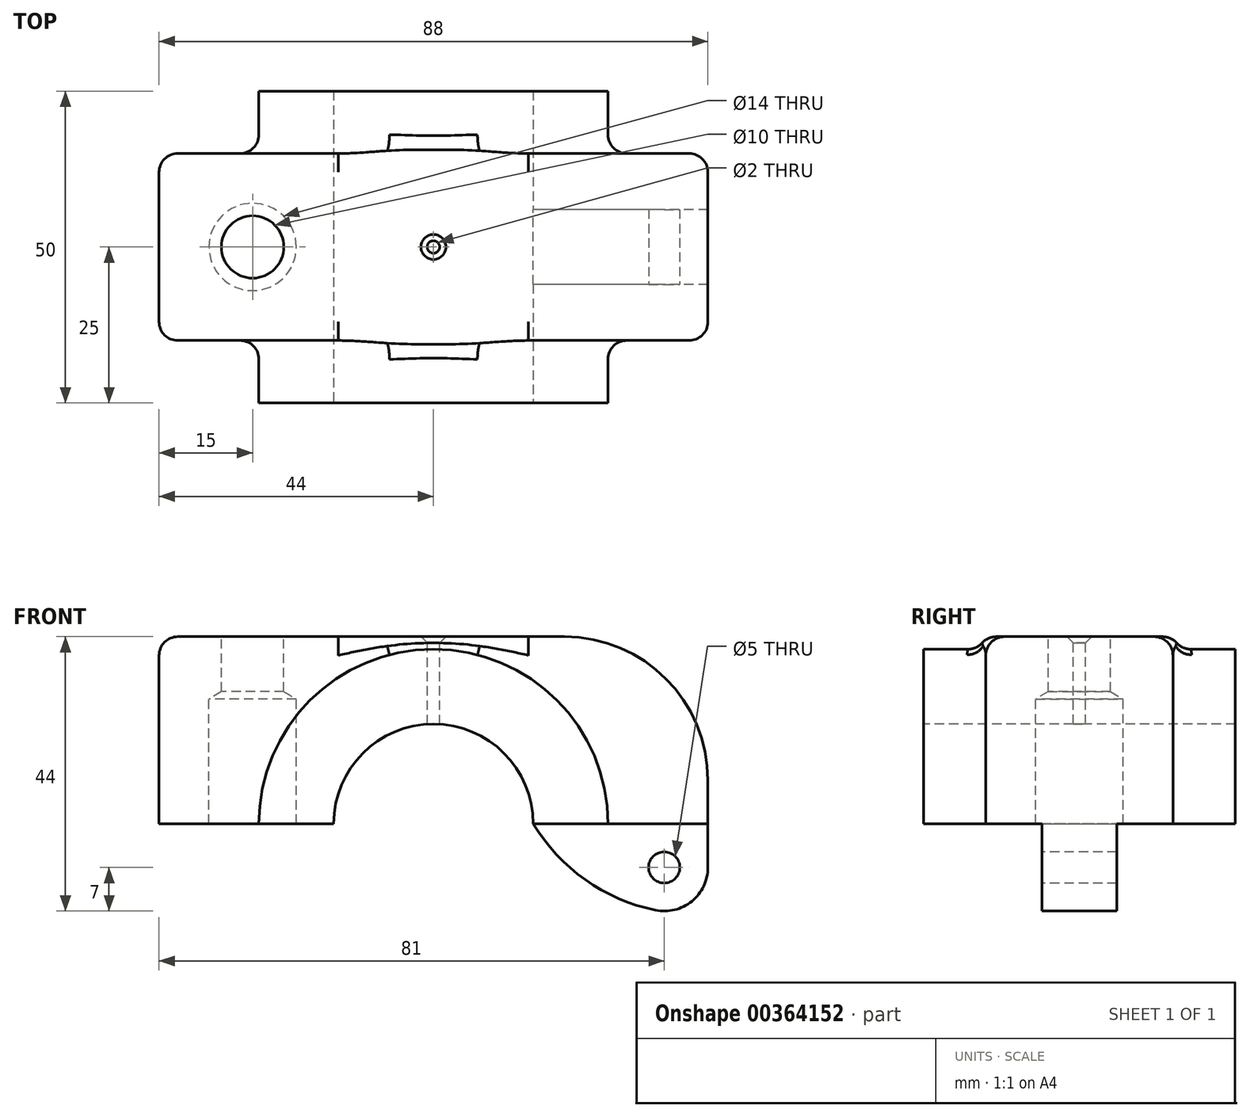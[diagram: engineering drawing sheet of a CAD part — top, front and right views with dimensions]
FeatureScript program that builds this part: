
annotation { "Feature Type Name" : "Feature", "Feature Type Description" : "" }
export const myFeature = defineFeature(function(context is Context, id is Id, definition is map)
    precondition{}
    {
        {
            var Q0;
            Q0=qCreatedBy(makeId("Front.planeOp"),FACE);
            var sketch = newSketch(context, id + "F0", { "sketchPlane" : qUnion([Q0])});
            skLineSegment(sketch, "E0", {"start": v(-44, 0) * mm, "end": v(-44, 30) * mm});
            skLineSegment(sketch, "E1", {"start": v(-44, 30) * mm, "end": v(44, 30) * mm});
            skLineSegment(sketch, "E2", {"start": v(44, 30) * mm, "end": v(44, -7) * mm});
            skLineSegment(sketch, "E3", {"start": v(-44, 0) * mm, "end": v(16, 0) * mm});
            skArc(sketch, "E4", {"start": v(44, -7) * mm, "mid": v(41.42, -12.43) * mm, "end": v(35.58, -13.85) * mm});
            skArc(sketch, "E5", {"start": v(35.58, -13.85) * mm, "mid": v(24.34, -8.97) * mm, "end": v(16, 0) * mm});
            skSolve(sketch);
        }
        {
            var Q0;
            Q0=makeQuery(id+"F0.imprint","IMPRINT",FACE,{"disambiguationData":[TD([[makeQuery(id+"F0.imprint","IMPRINT",EDGE,{"derivedFrom":sQuery(id+"F0.wireOp",EDGE,"E0")}),-1.0]])]});
            extrude(context, id + "F1", {"entities" : qUnion([Q0]), "depth" : 15 * mm, "hasSecondDirection" : true, "secondDirectionOppositeDirection" : true, "secondDirectionDepth" : 15 * mm});
        }
        {
            var Q0;
            Q0=qCreatedBy(makeId("Front.planeOp"),FACE);
            var sketch = newSketch(context, id + "F2", { "sketchPlane" : qUnion([Q0])});
            skArc(sketch, "E6", {"start": v(-28, 0) * mm, "mid": v(0, 28) * mm, "end": v(28, 0) * mm});
            skLineSegment(sketch, "E7", {"start": v(-28, 0) * mm, "end": v(28, 0) * mm});
            skSolve(sketch);
        }
        {
            var Q0;
            Q0=qCreatedBy(makeId("Right.planeOp"),FACE);
            var sketch = newSketch(context, id + "F3", { "sketchPlane" : qUnion([Q0])});
            skLineSegment(sketch, "E8.bottom", {"start": v(-6, 0) * mm, "end": v(-20, 0) * mm});
            skLineSegment(sketch, "E8.top", {"start": v(-6, -20) * mm, "end": v(-20, -20) * mm});
            skLineSegment(sketch, "E8.left", {"start": v(-6, 0) * mm, "end": v(-6, -20) * mm});
            skLineSegment(sketch, "E8.right", {"start": v(-20, 0) * mm, "end": v(-20, -20) * mm});
            skLineSegment(sketch, "E9.MirrorCS", {"start": v(6, -20) * mm, "end": v(20, -20) * mm});
            skLineSegment(sketch, "E10.MirrorCS", {"start": v(20, 0) * mm, "end": v(20, -20) * mm});
            skLineSegment(sketch, "E11.MirrorCS", {"start": v(6, 0) * mm, "end": v(20, 0) * mm});
            skLineSegment(sketch, "E12.MirrorCS", {"start": v(6, 0) * mm, "end": v(6, -20) * mm});
            skSolve(sketch);
        }
        {
            var Q0;
            Q0=makeQuery(id+"F3.imprint","IMPRINT",FACE,{"disambiguationData":[TD([[makeQuery(id+"F3.imprint","IMPRINT",EDGE,{"derivedFrom":sQuery(id+"F3.wireOp",EDGE,"E9.MirrorCS")}),1.0]])]});
            var Q1;
            Q1=makeQuery(id+"F3.imprint","IMPRINT",FACE,{"disambiguationData":[TD([[makeQuery(id+"F3.imprint","IMPRINT",EDGE,{"derivedFrom":sQuery(id+"F3.wireOp",EDGE,"E8.bottom")}),1.0]])]});
            extrude(context, id + "F4", {"entities" : qUnion([Q0, Q1]), "operationType" : NewBodyOperationType.REMOVE, "endBound" : BoundingType.THROUGH_ALL, "depth" : 25 * mm});
        }
        {
            var Q0;
            Q0 = qSketchRegion(id + "F2", true);
            extrude(context, id + "F5", {"entities" : qUnion([Q0]), "operationType" : NewBodyOperationType.ADD, "depth" : 25 * mm, "hasSecondDirection" : true, "secondDirectionOppositeDirection" : true, "secondDirectionDepth" : 25 * mm});
        }
        {
            var Q0;
            Q0=qCreatedBy(makeId("Front.planeOp"),FACE);
            var sketch = newSketch(context, id + "F6", { "sketchPlane" : qUnion([Q0])});
            skCircle(sketch, "E13", {"center": v(0, 0) * mm, "radius": 16 * mm});
            skSolve(sketch);
        }
        {
            var Q0;
            Q0=makeQuery(id+"F6.imprint","IMPRINT",FACE,{"disambiguationData":[TD([[makeQuery(id+"F6.imprint","IMPRINT",EDGE,{"derivedFrom":sQuery(id+"F6.wireOp",EDGE,"E13")}),1.0]])]});
            extrude(context, id + "F7", {"entities" : qUnion([Q0]), "operationType" : NewBodyOperationType.REMOVE, "endBound" : BoundingType.THROUGH_ALL, "oppositeDirection" : true, "depth" : 25 * mm, "hasSecondDirection" : true, "secondDirectionOppositeDirection" : false, "secondDirectionDepth" : 25 * mm});
        }
        {
            var Q0;
            Q0=qCreatedBy(makeId("Front.planeOp"),FACE);
            var sketch = newSketch(context, id + "F8", { "sketchPlane" : qUnion([Q0])});
            skLineSegment(sketch, "E14", {"start": v(-29, 35.4) * mm, "end": v(-29, -6) * mm, "construction": true});
            skLineSegment(sketch, "E15", {"start": v(-29, 32) * mm, "end": v(-24, 32) * mm});
            skLineSegment(sketch, "E16", {"start": v(-24, 32) * mm, "end": v(-24, 21.2) * mm});
            skLineSegment(sketch, "E17", {"start": v(-24, 21.2) * mm, "end": v(-22, 20) * mm});
            skLineSegment(sketch, "E18", {"start": v(-22, 20) * mm, "end": v(-22, -2) * mm});
            skLineSegment(sketch, "E19", {"start": v(-22, -2) * mm, "end": v(-29, -2) * mm});
            skLineSegment(sketch, "E20", {"start": v(-29, 32) * mm, "end": v(-29, -2) * mm});
            skSolve(sketch);
        }
        {
            var Q0;
            Q0=makeQuery(id+"F8.imprint","IMPRINT",FACE,{"disambiguationData":[TD([[makeQuery(id+"F8.imprint","IMPRINT",EDGE,{"derivedFrom":sQuery(id+"F8.wireOp",EDGE,"E15")}),-1.0]])]});
            var Q1;
            Q1=sQuery(id+"F8.wireOp",EDGE,"E14");
            revolve(context, id + "F9", {"entities" : qUnion([Q0]), "axis" : qUnion([Q1]), "revolveType" : RevolveType.FULL});
        }
        {
            var Q0;
            Q0=makeQuery(id+"F9.opRevolve","SWEPT_BODY",BODY,{"disambiguationData":[OSD([sQuery(id+"F8.wireOp",EDGE,"E15"),sQuery(id+"F8.wireOp",EDGE,"E16"),sQuery(id+"F8.wireOp",EDGE,"E17"),sQuery(id+"F8.wireOp",EDGE,"E18"),sQuery(id+"F8.wireOp",EDGE,"E19"),sQuery(id+"F8.wireOp",EDGE,"E20")])]});
            var Q1;
            Q1=makeQuery(id+"F1.opExtrude","SWEPT_BODY",BODY,{"disambiguationData":[OSD([sQuery(id+"F0.wireOp",EDGE,"E0"),sQuery(id+"F0.wireOp",EDGE,"E1"),sQuery(id+"F0.wireOp",EDGE,"E2"),sQuery(id+"F0.wireOp",EDGE,"E3"),sQuery(id+"F0.wireOp",EDGE,"E4"),sQuery(id+"F0.wireOp",EDGE,"E5")])]});
            booleanBodies(context, id + "F10", {"operationType" : BooleanOperationType.SUBTRACTION, "tools" : qUnion([Q0]), "targets" : qUnion([Q1])});
        }
        {
            var Q0;
            Q0=makeQuery(id+"F1.opExtrude","SWEPT_FACE",FACE,{"disambiguationData":[OSD([sQuery(id+"F0.wireOp",EDGE,"E1")])]});
            var sketch = newSketch(context, id + "F11", { "sketchPlane" : qUnion([Q0])});
            skPoint(sketch, "E21", {"position": v(0, 0) * mm});
            skSolve(sketch);
        }
        {
            var Q0;
            Q0=sQuery(id+"F11.wireOp",VERTEX,"E21");
            var Q1;
            Q1=makeQuery(id+"F1.opExtrude","SWEPT_BODY",BODY,{"disambiguationData":[OSD([sQuery(id+"F0.wireOp",EDGE,"E0"),sQuery(id+"F0.wireOp",EDGE,"E1"),sQuery(id+"F0.wireOp",EDGE,"E2"),sQuery(id+"F0.wireOp",EDGE,"E3"),sQuery(id+"F0.wireOp",EDGE,"E4"),sQuery(id+"F0.wireOp",EDGE,"E5")])]});
            hole(context, id + "F12", {"style" : HoleStyle.C_SINK, "endStyle" : HoleEndStyle.THROUGH, "standardTappedOrClearance" : lookupTablePath({ "standard" : "Custom", "fit" : "Normal", "size" : "M5", "type" : "Clearance" }), "standardBlindInLast" : lookupTablePath({ "fit" : "Standard", "standard" : "Custom", "size" : "M5", "type" : "Clearance" }), "holeDiameter" : 2 * mm, "cSinkDiameter" : 4 * mm, "cSinkAngle" : 90 * degree, "isTappedThrough" : true, "tappedDepth" : 12 * mm, "tapClearance" : 3, "locations" : qUnion([Q0]), "scope" : qUnion([Q1])});
        }
        {
            var Q0;
            Q0=makeQuery(id+"F4.boolean.opBoolean","COPY",FACE,{"derivedFrom":makeQuery(id+"F4.opExtrude","SWEPT_FACE",FACE,{"disambiguationData":[OSD([sQuery(id+"F3.wireOp",EDGE,"E8.left")])]})});
            var sketch = newSketch(context, id + "F13", { "sketchPlane" : qUnion([Q0])});
            skPoint(sketch, "E22", {"position": v(37, -7) * mm});
            skSolve(sketch);
        }
        {
            var Q0;
            Q0=sQuery(id+"F13.wireOp",VERTEX,"E22");
            var Q1;
            Q1=makeQuery(id+"F1.opExtrude","SWEPT_BODY",BODY,{"disambiguationData":[OSD([sQuery(id+"F0.wireOp",EDGE,"E0"),sQuery(id+"F0.wireOp",EDGE,"E1"),sQuery(id+"F0.wireOp",EDGE,"E2"),sQuery(id+"F0.wireOp",EDGE,"E3"),sQuery(id+"F0.wireOp",EDGE,"E4"),sQuery(id+"F0.wireOp",EDGE,"E5")])]});
            hole(context, id + "F14", {"style" : HoleStyle.SIMPLE, "endStyle" : HoleEndStyle.THROUGH, "holeDiameter" : 5 * mm, "isTappedThrough" : true, "tappedDepth" : 12 * mm, "tapClearance" : 3, "locations" : qUnion([Q0]), "scope" : qUnion([Q1])});
        }
        {
            var Q0;
            Q0=makeQuery(id+"F1.opExtrude","SWEPT_EDGE",EDGE,{"disambiguationData":[OSD([sQuery(id+"F0.wireOp",EDGE,"E1"),sQuery(id+"F0.wireOp",EDGE,"E2")])]});
            fillet(context, id + "F15", {"entities" : qUnion([Q0]), "radius" : 23 * mm, "tangentPropagation" : true, "allowEdgeOverflow" : false});
        }
        {
            var Q0;
            Q0=makeQuery(id+"F1.opExtrude","SWEPT_EDGE",EDGE,{"disambiguationData":[OSD([sQuery(id+"F0.wireOp",EDGE,"E0"),sQuery(id+"F0.wireOp",EDGE,"E1")])]});
            fillet(context, id + "F16", {"entities" : qUnion([Q0]), "radius" : 3 * mm, "tangentPropagation" : true, "allowEdgeOverflow" : false});
        }
        {
            var Q0;
            Q0=makeQuery(id+"F5.boolean.opBoolean","INTERSECT",EDGE,{"derivedFrom":[makeQuery(id+"F1.opExtrude","CAP_FACE",FACE,{"disambiguationData":[OSD([sQuery(id+"F0.wireOp",EDGE,"E0"),sQuery(id+"F0.wireOp",EDGE,"E1"),sQuery(id+"F0.wireOp",EDGE,"E2"),sQuery(id+"F0.wireOp",EDGE,"E3"),sQuery(id+"F0.wireOp",EDGE,"E4"),sQuery(id+"F0.wireOp",EDGE,"E5")])],"isStart":false}),makeQuery(id+"F5.opExtrude","SWEPT_FACE",FACE,{"disambiguationData":[OSD([sQuery(id+"F2.wireOp",EDGE,"E6")])]})]});
            var Q1;
            Q1=makeQuery(id+"F5.boolean.opBoolean","INTERSECT",EDGE,{"derivedFrom":[makeQuery(id+"F1.opExtrude","CAP_FACE",FACE,{"disambiguationData":[OSD([sQuery(id+"F0.wireOp",EDGE,"E0"),sQuery(id+"F0.wireOp",EDGE,"E1"),sQuery(id+"F0.wireOp",EDGE,"E2"),sQuery(id+"F0.wireOp",EDGE,"E3"),sQuery(id+"F0.wireOp",EDGE,"E4"),sQuery(id+"F0.wireOp",EDGE,"E5")])],"isStart":true}),makeQuery(id+"F5.opExtrude","SWEPT_FACE",FACE,{"disambiguationData":[OSD([sQuery(id+"F2.wireOp",EDGE,"E6")])]})]});
            fillet(context, id + "F17", {"entities" : qUnion([Q0, Q1]), "radius" : 3 * mm, "tangentPropagation" : true, "allowEdgeOverflow" : false});
        }
        {
            var Q0;
            {var subQ0=sQuery(id+"F0.wireOp",EDGE,"E2");var subQ1=sQuery(id+"F0.wireOp",EDGE,"E1");Q0=makeQuery(id+"F15.opFillet","BLEND_EDGE",EDGE,{"blendedFrom":[makeQuery(id+"F1.opExtrude","SWEPT_EDGE",EDGE,{"disambiguationData":[OSD([subQ1,subQ0])]}),makeQuery(id+"F1.opExtrude","CAP_FACE",FACE,{"disambiguationData":[OSD([sQuery(id+"F0.wireOp",EDGE,"E0"),subQ1,subQ0,sQuery(id+"F0.wireOp",EDGE,"E3"),sQuery(id+"F0.wireOp",EDGE,"E4"),sQuery(id+"F0.wireOp",EDGE,"E5")])],"isStart":false})],"blendedInto":[makeQuery(id+"F1.opExtrude","CAP_FACE",FACE,{"disambiguationData":[OSD([sQuery(id+"F0.wireOp",EDGE,"E0"),subQ1,subQ0,sQuery(id+"F0.wireOp",EDGE,"E3"),sQuery(id+"F0.wireOp",EDGE,"E4"),sQuery(id+"F0.wireOp",EDGE,"E5")])],"isStart":false})]});}
            var Q1;
            {var subQ0=sQuery(id+"F0.wireOp",EDGE,"E2");var subQ1=sQuery(id+"F0.wireOp",EDGE,"E1");Q1=makeQuery(id+"F15.opFillet","BLEND_EDGE",EDGE,{"blendedFrom":[makeQuery(id+"F1.opExtrude","SWEPT_EDGE",EDGE,{"disambiguationData":[OSD([subQ1,subQ0])]}),makeQuery(id+"F1.opExtrude","CAP_FACE",FACE,{"disambiguationData":[OSD([sQuery(id+"F0.wireOp",EDGE,"E0"),subQ1,subQ0,sQuery(id+"F0.wireOp",EDGE,"E3"),sQuery(id+"F0.wireOp",EDGE,"E4"),sQuery(id+"F0.wireOp",EDGE,"E5")])],"isStart":true})],"blendedInto":[makeQuery(id+"F1.opExtrude","CAP_FACE",FACE,{"disambiguationData":[OSD([sQuery(id+"F0.wireOp",EDGE,"E0"),subQ1,subQ0,sQuery(id+"F0.wireOp",EDGE,"E3"),sQuery(id+"F0.wireOp",EDGE,"E4"),sQuery(id+"F0.wireOp",EDGE,"E5")])],"isStart":true})]});}
            fillet(context, id + "F18", {"entities" : qUnion([Q0, Q1]), "radius" : 3 * mm, "tangentPropagation" : true, "allowEdgeOverflow" : false});
        }
    });
